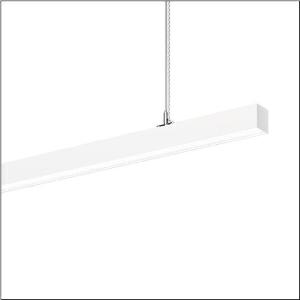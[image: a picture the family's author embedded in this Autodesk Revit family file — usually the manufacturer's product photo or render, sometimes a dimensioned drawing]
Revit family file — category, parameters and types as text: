
# Revit family: silica_r__21_51mx33dc4dwb_294c
name_source: partatom
category: Lighting Fixtures
units: mm (PartAtom-declared; Revit-internal decimal feet)

## family parameters
Cut with Voids When Loaded = No
Host = Face
Light Source = No
Part Type = Normal
Room Calculation Point = No
Round Connector Dimension = Use Diameter
Shared = No

## types (1)
- --- (1 x LED, 14790 lm, 93.9 W, 4000K)
    Apparent Load = 94 VA
    CIE Flux Codes = 78 96 99 55 100
    Color Rendering = 80
    Color Temperature = 4000K
    Default Elevation = 1800 mm
    Description = Silica® 21, office luminaire, primary optical cover: prismatic diffuser, of PMMA, CAT 2 (L<= 3000cd/m²), light emission: direct/indirect distribution, primary light characteristic: symmetric, installation type: suspended mounting, LED, rated luminous flux: 14.790lm, luminous efficacy: 158lm/W, light colour: 840, colour temperature: 4000K, with terminal, 3+2-pole, max. 2.5mm², mains connection: 220..240V, AC, 50/60Hz, rated input power: 93.9W, luminaire housing, of aluminium, traffic white (RAL 9016), length: 3.004mm, width: 53mm, height: 53mm, protection rating (complete): IP20, insulation class (complete): insulation class I (protective earthing), certification: CE, permissible operating ambient temperature: 0..+35°C, standard: EN 50419, packaging unit: 1 piece
    Height = 53 mm
    Lamp = 1 x LED
    Lamp Light Flux = 14790 lm
    Lamp Power = 93.9 W
    Lamp count = 1
    Length = 3004 mm
    Luminous efficacy = 158 lm/W
    Manufacturer = Siteco
    ModVariant = No
    Model = 51MX33DC4DWB
    Mounting Place = Ceiling
    Mounting Type = Pendant
    Number of Poles = 1
    OnlyDefault = Yes
    Power Factor = 1
    Product Name = Silica® 21
    Product group = office luminaire | ceiling pendant
    ProductGroupID = 902
    Protection Class = Protection class I
    Protection Degree = IP 20
    RLX_Detail_Level = 1
    RLX_Emergency_Light_Flux = 0 lm
    RLX_Emergency_Type = 0
    RLX_Emergency_Type_DB = No
    RlxData = <blob elided: 21381 chars, md5=756ffd29>
    Socket = socket
    Standby Power = 0 W
    System Light Flux = 14790 lm
    System Power = 94 W
    Type Comments = factory setting: luminous flux: 100 % | dim-lin: 254 | 323 mA
    Type Image = l_1335916.jpg
    URL = http://relux.com
    VarID = @adj_088003
    Voltage = 0 V
    Weight = 0.00 kg
    Width = 53 mm

## geometry (parser evidence)
native form markers: Blend x4, Sweep x14
no freeform markers — native parametric forms only
